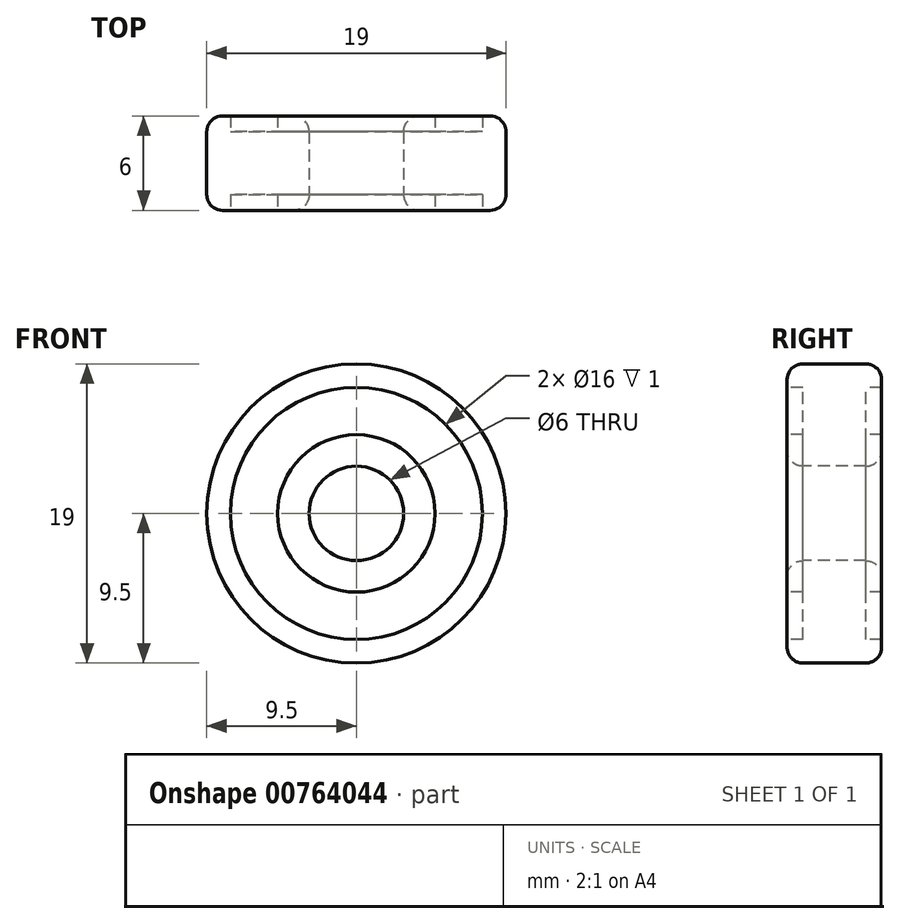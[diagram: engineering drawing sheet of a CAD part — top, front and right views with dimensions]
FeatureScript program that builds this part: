
annotation { "Feature Type Name" : "Feature", "Feature Type Description" : "" }
export const myFeature = defineFeature(function(context is Context, id is Id, definition is map)
    precondition{}
    {
        {
            var Q0;
            Q0=qCreatedBy(makeId("Right.planeOp"),FACE);
            var sketch = newSketch(context, id + "F0", { "sketchPlane" : qUnion([Q0])});
            skLineSegment(sketch, "E0.bottom", {"start": v(1, 9.5) * mm, "end": v(5, 9.5) * mm});
            skLineSegment(sketch, "E0.top", {"start": v(1, 3) * mm, "end": v(5, 3) * mm});
            skLineSegment(sketch, "E0.left", {"start": v(0, 8.5) * mm, "end": v(0, 8) * mm});
            skLineSegment(sketch, "E0.right", {"start": v(6, 8.5) * mm, "end": v(6, 8) * mm});
            skLineSegment(sketch, "E1.bottom", {"start": v(0, 8) * mm, "end": v(1, 8) * mm});
            skLineSegment(sketch, "E1.top", {"start": v(0, 5) * mm, "end": v(1, 5) * mm});
            skLineSegment(sketch, "E1.right", {"start": v(1, 8) * mm, "end": v(1, 5) * mm});
            skLineSegment(sketch, "E2.bottom", {"start": v(6, 8) * mm, "end": v(5, 8) * mm});
            skLineSegment(sketch, "E2.top", {"start": v(6, 5) * mm, "end": v(5, 5) * mm});
            skLineSegment(sketch, "E2.right", {"start": v(5, 8) * mm, "end": v(5, 5) * mm});
            skLineSegment(sketch, "E3.trimOffspring", {"start": v(0, 5) * mm, "end": v(0, 4) * mm});
            skLineSegment(sketch, "E4.trimOffspring", {"start": v(6, 5) * mm, "end": v(6, 4) * mm});
            skPoint(sketch, "E5.visualSharp", {"position": v(0, 9.5) * mm});
            skArc(sketch, "E5.filletArc", {"start": v(1, 9.5) * mm, "mid": v(0.3, 9.2) * mm, "end": v(0, 8.5) * mm});
            skPoint(sketch, "E6.visualSharp", {"position": v(6, 9.5) * mm});
            skArc(sketch, "E6.filletArc", {"start": v(6, 8.5) * mm, "mid": v(5.7, 9.2) * mm, "end": v(5, 9.5) * mm});
            skPoint(sketch, "E7.visualSharp", {"position": v(6, 3) * mm});
            skArc(sketch, "E7.filletArc", {"start": v(5, 3) * mm, "mid": v(5.7, 3.3) * mm, "end": v(6, 4) * mm});
            skPoint(sketch, "E8.visualSharp", {"position": v(0, 3) * mm});
            skArc(sketch, "E8.filletArc", {"start": v(0, 4) * mm, "mid": v(0.3, 3.3) * mm, "end": v(1, 3) * mm});
            skLineSegment(sketch, "E9", {"start": v(0, 0) * mm, "end": v(10.25, 0) * mm, "construction": true});
            skSolve(sketch);
        }
        {
            var Q0;
            Q0=makeQuery(id+"F0.imprint","IMPRINT",FACE,{"disambiguationData":[TD([[makeQuery(id+"F0.imprint","IMPRINT",EDGE,{"derivedFrom":sQuery(id+"F0.wireOp",EDGE,"E0.bottom")}),-1.0]])]});
            var Q1;
            Q1=sQuery(id+"F0.wireOp",EDGE,"E9");
            revolve(context, id + "F1", {"surfaceOperationType" : NewSurfaceOperationType.NEW, "entities" : qUnion([Q0]), "axis" : qUnion([Q1]), "revolveType" : RevolveType.FULL});
        }
    });
